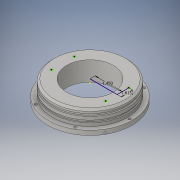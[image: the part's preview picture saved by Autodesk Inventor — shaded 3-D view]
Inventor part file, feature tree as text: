
AUTODESK INVENTOR PART (.ipt)
format: ipt  version: 2016 (Build 200138000, 138)  size: 345,088 bytes
history: native  units: in
note: dims shown in document units (in); Inventor stores cm internally (conversion verified against a paired STEP export)
features: sketch x24, extrude x20, plane x3, chamfer x2, fillet x1, revolve x1
ambient origin geometry x8: Origin, YZ Plane, XZ Plane, XY Plane, X Axis, Y Axis, Z Axis, Center Point
bodies: Solid1 (feature_tree)
feature tree (51):
  extrude  "Extrusion1"  Depth=0.3in TaperAngle=0.0deg
  extrude  "Extrusion2"  Depth=0.125in TaperAngle=0.0deg
  extrude  "Extrusion3"  Depth=3.875in
  sketch  "Sketch4"  dims[d9=0.125in d10=0.0in d11=4.0in]
  extrude  "Extrusion4"  Depth=4.0in
  extrude  "Extrusion5"  Depth=0.2in
  extrude  "Extrusion6"  Depth=0.24in TaperAngle=45.0deg
  chamfer  "Chamfer1"  Distance=2.3622in Angle=360.0deg
  extrude  "Extrusion7"  Depth=0.24in
  extrude  "Extrusion8"  Depth=5.0in TaperAngle=0.0deg
  extrude  "Extrusion9"  Depth=0.375in TaperAngle=0.0deg
  extrude  "Extrusion10"  Depth=0.375in TaperAngle=0.0deg
  extrude  "Extrusion11"  Depth=0.5in
  sketch  "Sketch13"  dims[d39=20.0in d40=0.0in d41=0.5in]
  extrude  "Extrusion12"  Depth=0.15in
  chamfer  "Chamfer2"  Distance=1.1811in Angle=360.0deg
  fillet  "Fillet1"  Radius=0.125in
  plane  "Work Plane1"
  revolve  "Revolution1"  [1 undecoded]
  plane  "Work Plane3"
  extrude  "Extrusion13"  [1 undecoded]
  extrude  "Extrusion14"  Depth=0.118in
  extrude  "Extrusion15"  Depth=0.118in
  extrude  "Extrusion16"  Depth=0.74in
  extrude  "Extrusion17"  Depth=0.74in
  extrude  "Extrusion18"  Depth=0.25in
  extrude  "Extrusion19"  Depth=1.04in TaperAngle=0.0deg
  extrude  "Extrusion20"  Depth=0.4in
  sketch  "Sketch24"  dims[d75=0.5in d76=1.04in d77=0.0in d78=0.1181in d79=0.4in d80=0.0in d81=0.1181in d82=0.4in d83=0.0in d84=0.1181in d85=0.4in d86=0.0in d87=12.0in d88=12.0in d89=0.0in d90=0.0in d91=2.0in d92=0.0in d93=0.1181in d94=2.9in d95=0.1181in d96=0.1181in d97=0.1181in d98=1.229in d99=1.229in d100=0.4in d101=0.0in d102=1.45in d103=0.6145in]
  sketch  "Sketch1"  dims[d0=4.0in d1=0.3in d2=0.0in]
  sketch  "Sketch2"  dims[d3=3.875in d4=0.125in d5=0.0in]
  sketch  "Sketch3"  dims[d6=0.3in d7=0.0in d8=3.875in]
  sketch  "Sketch5"  dims[d12=0.2in d13=0.0in d14=4.5in]
  sketch  "Sketch6"  dims[d15=0.24in d16=0.0in d17=0.1in d18=0.125in d19=45.0deg]
  sketch  "Sketch7"  dims[d20=0.138in]
  sketch  "Sketch8"  dims[d21=2.125in d22=2.3622in d24=360.0deg]
  sketch  "Sketch9"  dims[d26=0.24in d27=0.0in d28=1.0in]
  sketch  "Sketch10"  dims[d29=0.1in d31=5.0in d32=0.0in]
  sketch  "Sketch11"  dims[d33=3.0in d34=0.375in d35=0.0in]
  sketch  "Sketch12"  dims[d36=1.0in d37=0.375in d38=0.0in]
  sketch  "Sketch14"  dims[d42=0.5in d43=0.15in d44=1.1811in d46=360.0deg]
  sketch  "Sketch15"  dims[d48=5.0in d49=0.2in d50=0.0in d51=0.0in]
  plane  "Work Plane2"
  sketch  "Sketch16"  dims[d52=0.125in d53=0.125in d54=45.0deg d55=0.125in]
  sketch  "Sketch17"  dims[d58=0.1in d59=1.527in]
  sketch  "Sketch18"  dims[d60=90.0deg d61=-4.125in]
  sketch  "Sketch19"  dims[d64=0.118in d65=0.118in]
  sketch  "Sketch20"  dims[d66=0.118in d67=0.118in]
  sketch  "Sketch21"  dims[d68=0.74in d69=0.74in]
  sketch  "Sketch22"  dims[d70=0.74in d71=0.74in]
  sketch  "Sketch23"  dims[d72=5.0in d73=0.0in d74=0.25in]
note: 2 required parameter values undecoded (feature->parameter linkage not recoverable at this tier; creation-order binding heuristic only, values carry confidence <= 0.55)